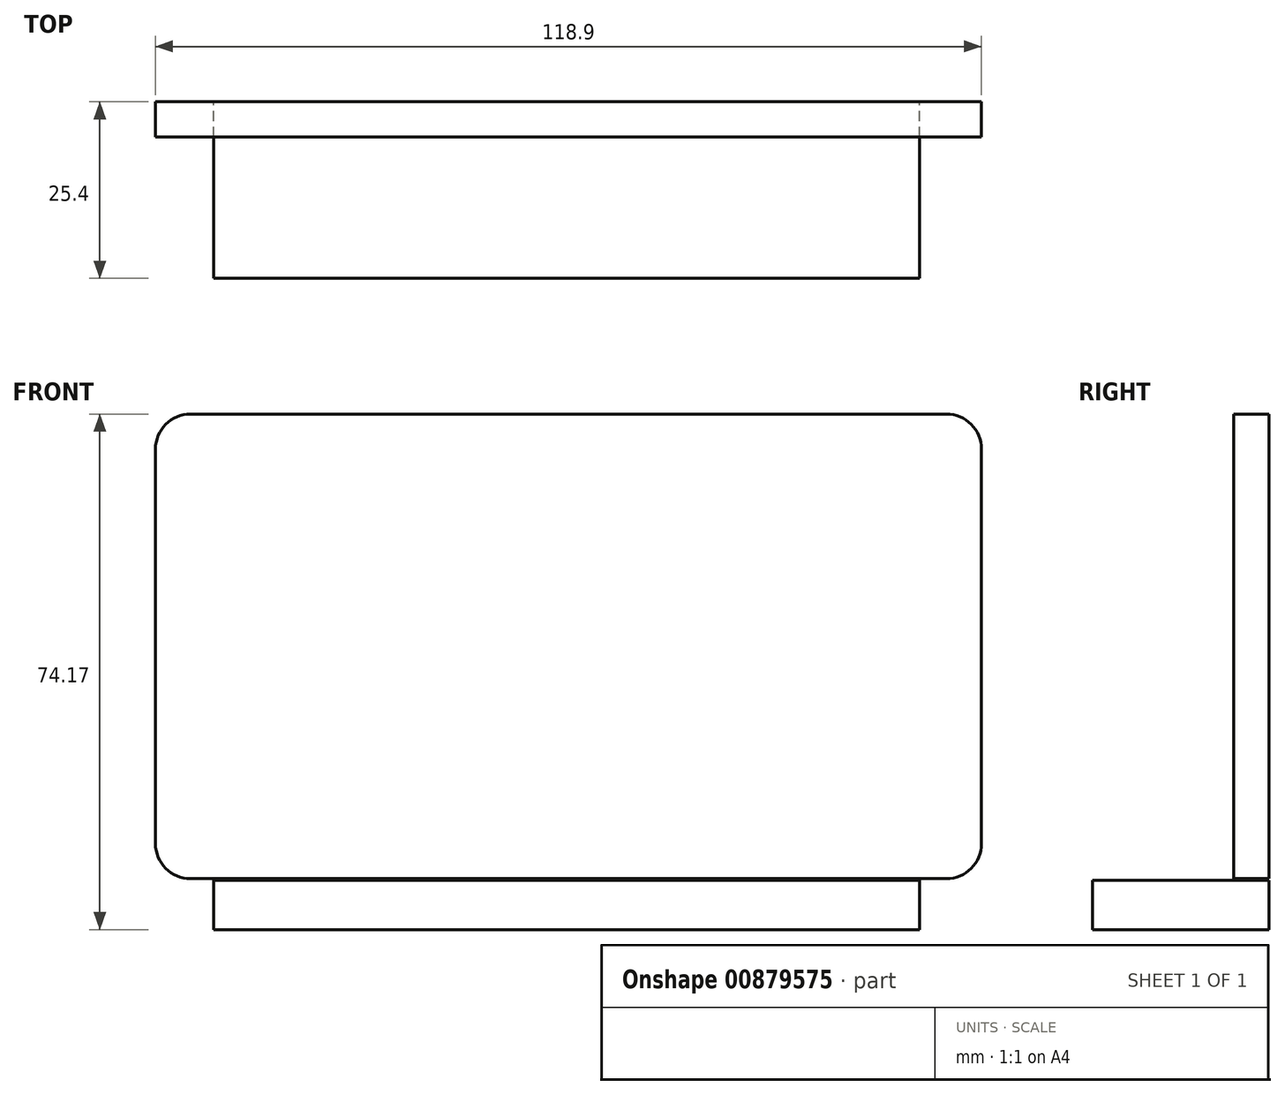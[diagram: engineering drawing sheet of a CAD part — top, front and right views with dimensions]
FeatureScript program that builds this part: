
annotation { "Feature Type Name" : "Feature", "Feature Type Description" : "" }
export const myFeature = defineFeature(function(context is Context, id is Id, definition is map)
    precondition{}
    {
        {
            var Q0;
            Q0=qCreatedBy(makeId("Front.planeOp"),FACE);
            var sketch = newSketch(context, id + "F0", { "sketchPlane" : qUnion([Q0])});
            skLineSegment(sketch, "E0.bottom", {"start": v(-59.17, 42.1) * mm, "end": v(59.73, 42.1) * mm});
            skLineSegment(sketch, "E0.top", {"start": v(-59.17, -24.76) * mm, "end": v(59.73, -24.76) * mm});
            skLineSegment(sketch, "E0.left", {"start": v(-59.17, 42.1) * mm, "end": v(-59.17, -24.76) * mm});
            skLineSegment(sketch, "E0.right", {"start": v(59.73, 42.1) * mm, "end": v(59.73, -24.76) * mm});
            skSolve(sketch);
        }
        {
            var Q0;
            Q0 = qSketchRegion(id + "F0", true);
            extrude(context, id + "F1", {"entities" : qUnion([Q0]), "depth" : 5.08 * mm, "offsetDistance" : 25.4 * mm});
        }
        {
            var Q0;
            Q0=makeQuery(id+"F1.opExtrude","SWEPT_EDGE",EDGE,{"disambiguationData":[OSD([sQuery(id+"F0.wireOp",EDGE,"E0.bottom"),sQuery(id+"F0.wireOp",EDGE,"E0.right")])]});
            var Q1;
            Q1=makeQuery(id+"F1.opExtrude","SWEPT_EDGE",EDGE,{"disambiguationData":[OSD([sQuery(id+"F0.wireOp",EDGE,"E0.bottom"),sQuery(id+"F0.wireOp",EDGE,"E0.left")])]});
            var Q2;
            Q2=makeQuery(id+"F1.opExtrude","SWEPT_EDGE",EDGE,{"disambiguationData":[OSD([sQuery(id+"F0.wireOp",EDGE,"E0.top"),sQuery(id+"F0.wireOp",EDGE,"E0.left")])]});
            var Q3;
            Q3=makeQuery(id+"F1.opExtrude","SWEPT_EDGE",EDGE,{"disambiguationData":[OSD([sQuery(id+"F0.wireOp",EDGE,"E0.top"),sQuery(id+"F0.wireOp",EDGE,"E0.right")])]});
            fillet(context, id + "F2", {"entities" : qUnion([Q0, Q1, Q2, Q3]), "radius" : 5.08 * mm, "tangentPropagation" : true, "allowEdgeOverflow" : false});
        }
        {
            var Q0;
            Q0=qCreatedBy(makeId("Front.planeOp"),FACE);
            var sketch = newSketch(context, id + "F3", { "sketchPlane" : qUnion([Q0])});
            skLineSegment(sketch, "E1.bottom", {"start": v(-50.8, -25) * mm, "end": v(50.8, -25) * mm});
            skLineSegment(sketch, "E1.top", {"start": v(-50.8, -32.07) * mm, "end": v(50.8, -32.07) * mm});
            skLineSegment(sketch, "E1.left", {"start": v(-50.8, -25) * mm, "end": v(-50.8, -32.07) * mm});
            skLineSegment(sketch, "E1.right", {"start": v(50.8, -25) * mm, "end": v(50.8, -32.07) * mm});
            skSolve(sketch);
        }
        {
            var Q0;
            Q0 = qSketchRegion(id + "F3", true);
            extrude(context, id + "F4", {"entities" : qUnion([Q0]), "depth" : 25.4 * mm, "offsetDistance" : 25.4 * mm});
        }
        {
            var Q0;
            Q0=makeQuery(id+"F4.opExtrude","CAP_EDGE",EDGE,{"disambiguationData":[OSD([sQuery(id+"F3.wireOp",EDGE,"E1.top")])],"isStart":false});
            fillet(context, id + "F5", {"entities" : qUnion([Q0]), "radius" : 5.08 * mm, "tangentPropagation" : true, "allowEdgeOverflow" : false});
        }
        {
            var Q0;
            Q0=makeQuery(id+"F4.opExtrude","CAP_EDGE",EDGE,{"disambiguationData":[OSD([sQuery(id+"F3.wireOp",EDGE,"E1.top")])],"isStart":true});
            var Q1;
            Q1=makeQuery(id+"F4.opExtrude","CAP_EDGE",EDGE,{"disambiguationData":[OSD([sQuery(id+"F3.wireOp",EDGE,"E1.left")])],"isStart":false});
            var Q2;
            Q2=makeQuery(id+"F4.opExtrude","CAP_EDGE",EDGE,{"disambiguationData":[OSD([sQuery(id+"F3.wireOp",EDGE,"E1.bottom")])],"isStart":false});
            fillet(context, id + "F6", {"entities" : qUnion([Q0, Q1, Q2]), "radius" : 5.08 * mm, "tangentPropagation" : true, "allowEdgeOverflow" : false});
        }
        {
            var Q0;
            Q0 = qSketchRegion(id + "F3", true);
            extrude(context, id + "F7", {"entities" : qUnion([Q0]), "operationType" : NewBodyOperationType.ADD, "depth" : 25.4 * mm, "offsetDistance" : 25.4 * mm});
        }
    });
